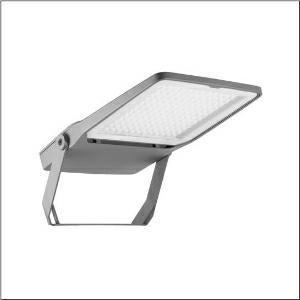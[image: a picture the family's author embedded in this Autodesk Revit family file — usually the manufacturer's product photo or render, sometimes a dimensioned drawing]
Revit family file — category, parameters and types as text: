
# Revit family: floodlight_fl_20_midi___pl52_5xa7682e2d1ac_b47e
name_source: partatom
category: Lighting Fixtures
units: mm (PartAtom-declared; Revit-internal decimal feet)

## family parameters
Cut with Voids When Loaded = No
Host = Face
Light Source = No
Part Type = Normal
Room Calculation Point = No
Round Connector Dimension = Use Diameter
Shared = No

## types (1)
- --- (1 x LED 4000K / CRI = 70 (unbekannt), 26840 lm, 4000K)
    Apparent Load = 208 VA
    CIE Flux Codes = 27 59 98 100 100
    Color Rendering = 70
    Color Temperature = 4000K
    Default Elevation = 1800 mm
    Description = Floodlight FL 20 midi, floodlight, primary light control with lens, of plastic, primary optical cover: protective disc, of toughened safety glass, transparent, light distribution: PL52, light emission: direct distribution, primary light characteristic: asymmetric, installation type: surface-mounted, LED High Power LED, rated luminous flux: 26.840 lm, light colour: 740, colour temperature: 4000K, control gear: ECG Plus, control: flexible luminous flux parameterisation, time-dependent luminous flux control, digital communication interface, power reduction, overheat protection, electronic power reduction, with terminal, 5-pole, max. 2.5mm², mains connection: 220..240V, AC, 50/60Hz, rated input power: 208W, LED unit, of diecast aluminium, powder-coated, Siteco® metallic grey (DB 702S), length: 654 mm, width: 450 mm, height: 76mm, housing frame, of diecast aluminium, powder-coated, Siteco® metallic grey (DB 702S), mounting bracket, of steel, powder-coated, Siteco® metallic grey (DB 702S), DALIprotection rating (complete): IP66, insulation class (complete): insulation class II (safety insulation), certification: CE, ENEC, VDE, protection symbol: D, permissible ambient temperature for indoor applications: -40..+40°C, permissible ambient temperature for outdoor applications: -40..+50°C, standard: DIN EN 12944, packaging unit: 1 piece

Light Distribution: PL52
    Height = 76 mm
    Lamp = 1 x LED 4000K / CRI >= 70 (unbekannt)
    Lamp Light Flux = 26840 lm
    Lamp count = 1
    Length = 672 mm
    Luminous efficacy = 129 lm/W
    Manufacturer = Siteco
    ModVariant = No
    Model = 5XA7682E2D1AC
    Number of Poles = 1
    OnlyDefault = Yes
    Power Factor = 1
    Product Name = Floodlight FL 20 midi | PL52
    Product group = floodlight | pylon top
    ProductGroupID = 6101
    Protection Class = Protection class II
    Protection Degree = IP 66
    RLX_Detail_Level = 1
    RlxData = <blob elided: 97661 chars, md5=b468f315>
    Socket = socket
    Standby Power = 0 W
    System Light Flux = 26840 lm
    System Power = 208 W
    Type Comments = factory setting: luminous flux: 100 % | dim-lin: 254 | 484 mA
    Type Image = l_1005943.jpg
    URL = http://relux.com
    VarID = @adj_142969
    Voltage = 0 V
    Weight = 0.00 kg
    Width = 450 mm

## geometry (parser evidence)
native form markers: Blend x4, Sweep x12
no freeform markers — native parametric forms only
